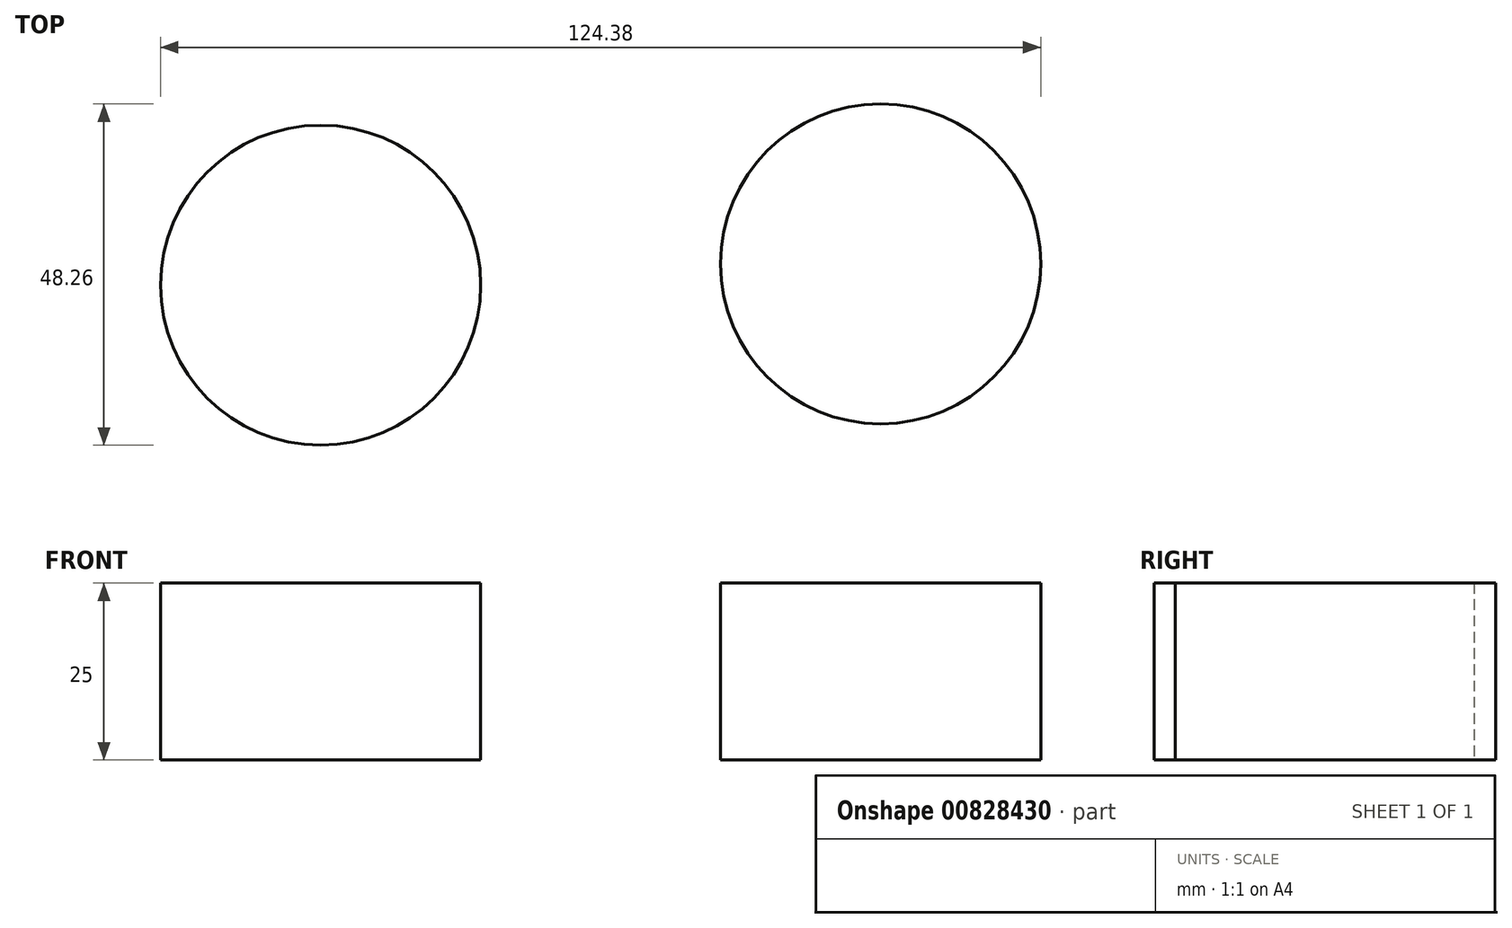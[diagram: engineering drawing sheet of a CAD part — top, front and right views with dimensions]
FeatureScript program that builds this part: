
annotation { "Feature Type Name" : "Feature", "Feature Type Description" : "" }
export const myFeature = defineFeature(function(context is Context, id is Id, definition is map)
    precondition{}
    {
        {
            var Q0;
            Q0=qCreatedBy(makeId("Top.planeOp"),FACE);
            var sketch = newSketch(context, id + "F0", { "sketchPlane" : qUnion([Q0])});
            skCircle(sketch, "E0", {"center": v(73.7, 2.57) * mm, "radius": 22.62 * mm});
            skCircle(sketch, "E1", {"center": v(-5.44, -0.43) * mm, "radius": 22.62 * mm});
            skLineSegment(sketch, "E2", {"start": v(73.7, 2.57) * mm, "end": v(-5.44, -0.43) * mm, "construction": true});
            skLineSegment(sketch, "E3", {"start": v(73.7, 2.57) * mm, "end": v(36.74, -67.46) * mm, "construction": true});
            skLineSegment(sketch, "E4", {"start": v(36.74, -67.46) * mm, "end": v(-5.44, -0.43) * mm, "construction": true});
            skSolve(sketch);
        }
        {
            var Q0;
            Q0 = qSketchRegion(id + "F0", true);
            extrude(context, id + "F1", {"entities" : qUnion([Q0]), "depth" : 25 * mm, "offsetDistance" : 25 * mm});
        }
    });
